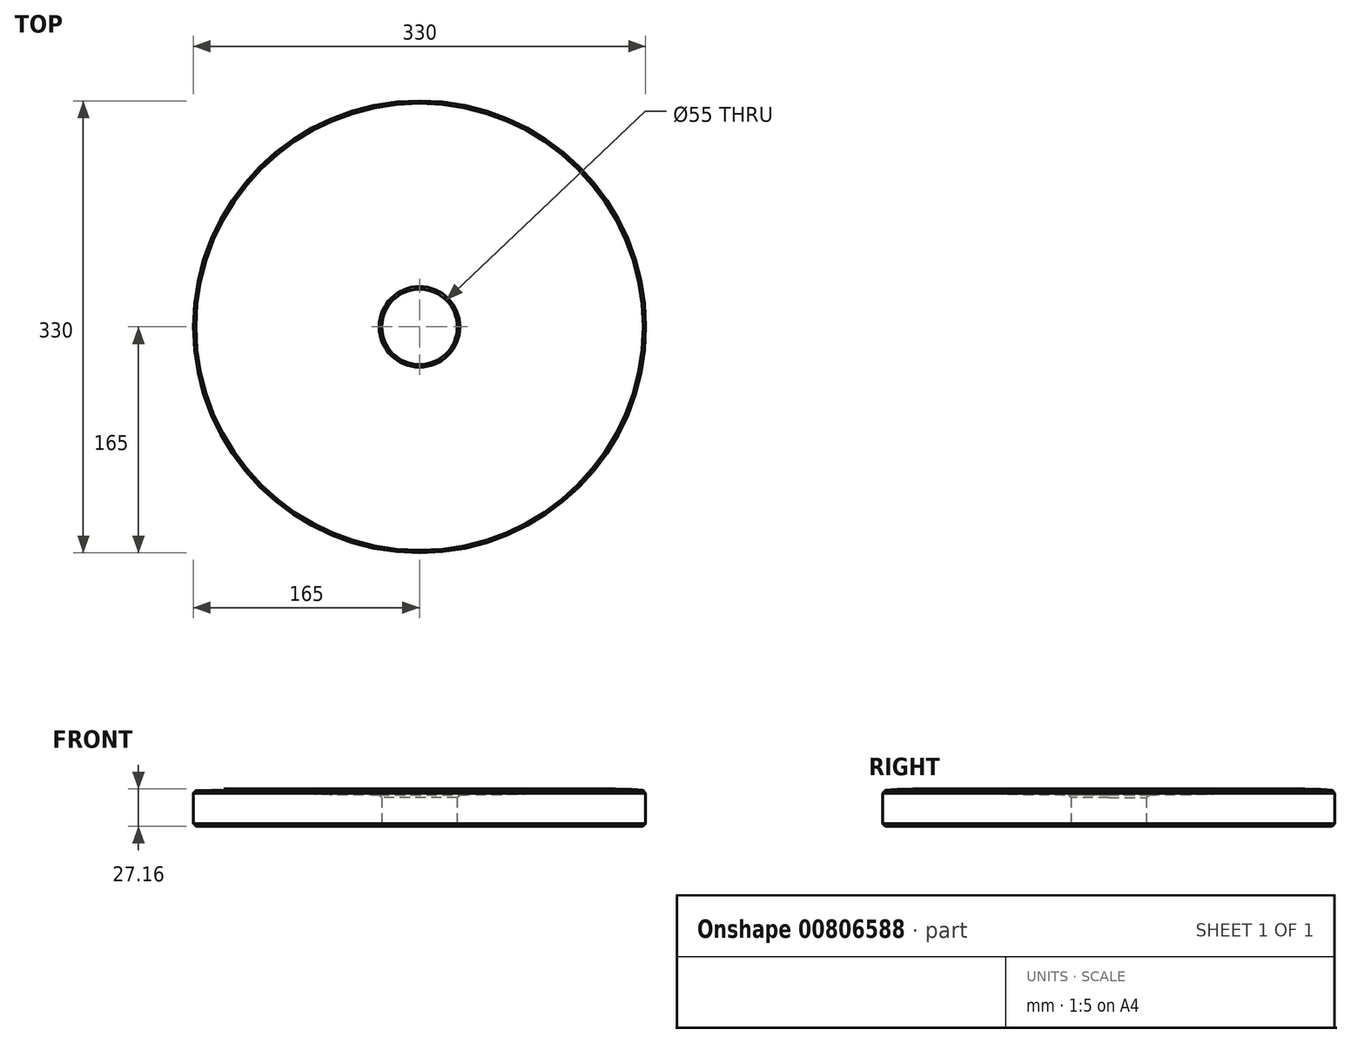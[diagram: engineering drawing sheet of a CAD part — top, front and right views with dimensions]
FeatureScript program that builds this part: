
annotation { "Feature Type Name" : "Feature", "Feature Type Description" : "" }
export const myFeature = defineFeature(function(context is Context, id is Id, definition is map)
    precondition{}
    {
        {
            var Q0;
            Q0=qCreatedBy(makeId("Front.planeOp"),FACE);
            var sketch = newSketch(context, id + "F0", { "sketchPlane" : qUnion([Q0])});
            skLineSegment(sketch, "E0", {"start": v(-27.5, 0) * mm, "end": v(-165, 0) * mm});
            skLineSegment(sketch, "E1", {"start": v(-165, 0) * mm, "end": v(-165, 26) * mm});
            skFitSpline(sketch, "E2", {"points": [v(-165, 26) * mm, v(-116.42, 26) * mm, v(-84.28, 23.9) * mm, v(-54.38, 23.18) * mm, v(-27.5, 23) * mm], "startDerivative": vector(188.04, 20.06) * mm, "endDerivative": vector(136.58, -0.3) * mm});
            skLineSegment(sketch, "E3", {"start": v(-27.5, 23) * mm, "end": v(-27.5, 0) * mm});
            skLineSegment(sketch, "E4", {"start": v(0, 0) * mm, "end": v(0, 36.5) * mm, "construction": true});
            skLineSegment(sketch, "E5", {"start": v(-156.7, 0) * mm, "end": v(-156.7, 28) * mm, "construction": true});
            skLineSegment(sketch, "E6", {"start": v(-156.7, 28) * mm, "end": v(-113.52, 28) * mm, "construction": true});
            skSolve(sketch);
        }
        {
            var Q0;
            Q0=makeQuery(id+"F0.imprint","IMPRINT",FACE,{"disambiguationData":[TD([[makeQuery(id+"F0.imprint","IMPRINT",EDGE,{"derivedFrom":sQuery(id+"F0.wireOp",EDGE,"E0")}),-1.0]])]});
            var Q1;
            Q1=sQuery(id+"F0.wireOp",EDGE,"E4");
            revolve(context, id + "F1", {"surfaceOperationType" : NewSurfaceOperationType.NEW, "entities" : qUnion([Q0]), "axis" : qUnion([Q1]), "revolveType" : RevolveType.FULL});
        }
        {
            var Q0;
            Q0=makeQuery(id+"F1.opRevolve","SWEPT_FACE",FACE,{"disambiguationData":[OSD([sQuery(id+"F0.wireOp",EDGE,"E1")])]});
            var Q1;
            Q1=makeQuery(id+"F1.opRevolve","SWEPT_FACE",FACE,{"disambiguationData":[OSD([sQuery(id+"F0.wireOp",EDGE,"E3")])]});
            chamfer(context, id + "F2", {"entities" : qUnion([Q0, Q1]), "width" : 2 * mm, "tangentPropagation" : true});
        }
    });
